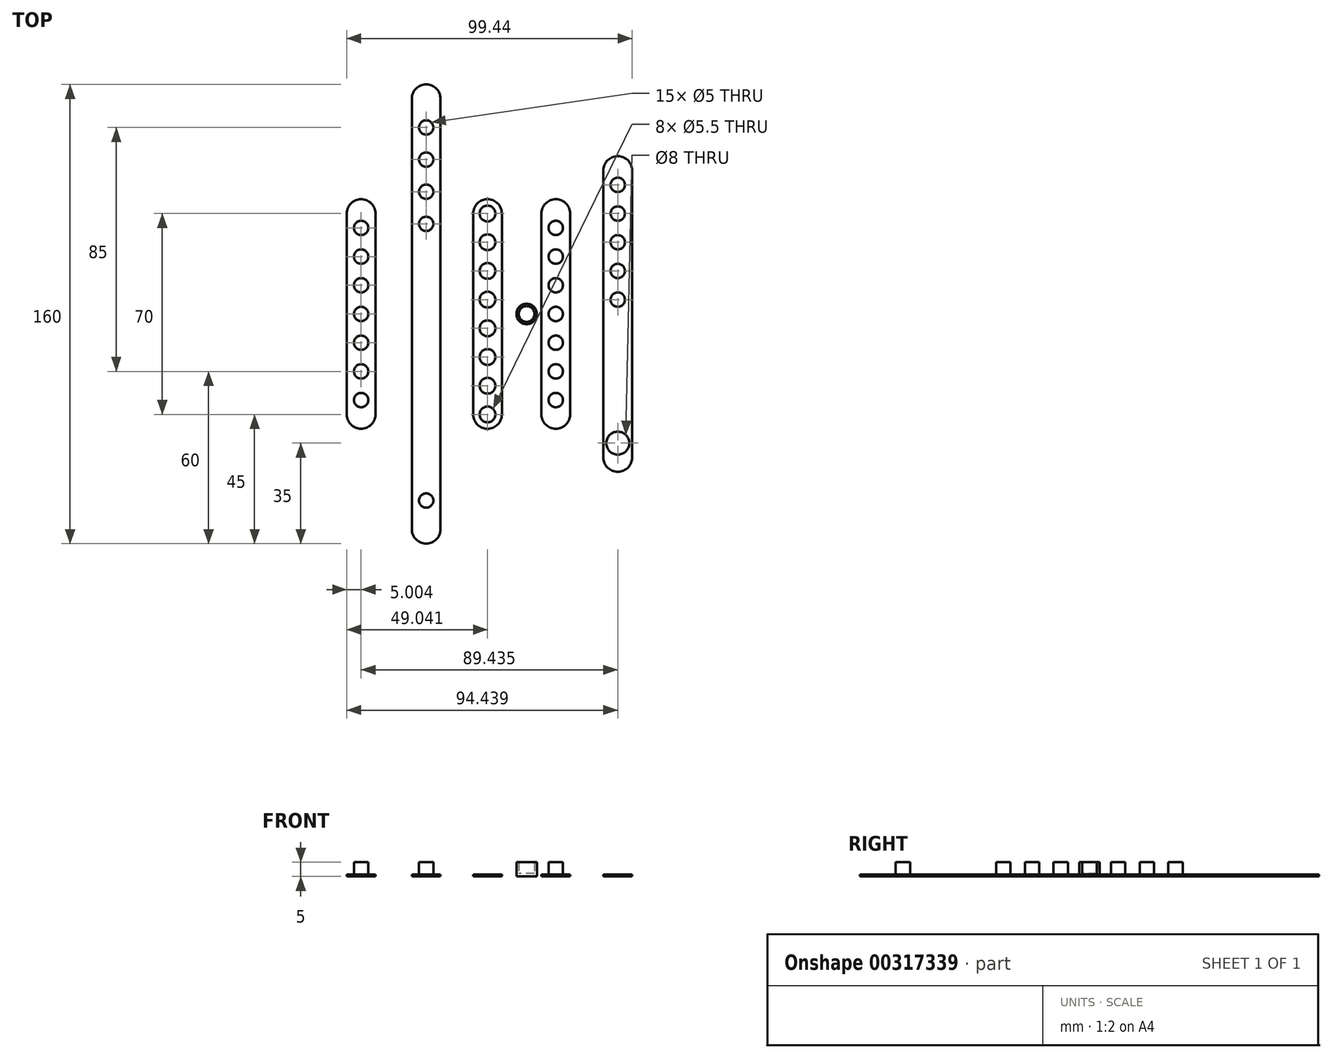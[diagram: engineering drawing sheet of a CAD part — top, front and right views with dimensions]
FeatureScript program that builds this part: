
annotation { "Feature Type Name" : "Feature", "Feature Type Description" : "" }
export const myFeature = defineFeature(function(context is Context, id is Id, definition is map)
    precondition{}
    {
        {
            var Q0;
            Q0=qCreatedBy(makeId("Top.planeOp"),FACE);
            var sketch = newSketch(context, id + "F0", { "sketchPlane" : qUnion([Q0])});
            skLineSegment(sketch, "E0", {"start": v(-40, 75) * mm, "end": v(-40, -75) * mm});
            skLineSegment(sketch, "E1", {"start": v(-40, -75) * mm, "end": v(-30, -75) * mm});
            skLineSegment(sketch, "E2", {"start": v(-30, -75) * mm, "end": v(-30, 75) * mm});
            skLineSegment(sketch, "E3", {"start": v(-30, 75) * mm, "end": v(-40, 75) * mm});
            skArc(sketch, "E4", {"start": v(-30, -75) * mm, "mid": v(-35, -80) * mm, "end": v(-40, -75) * mm});
            skArc(sketch, "E5", {"start": v(-30, 75) * mm, "mid": v(-35, 80) * mm, "end": v(-40, 75) * mm});
            skCircle(sketch, "E6", {"center": v(-35, -65) * mm, "radius": 2.5 * mm});
            skCircle(sketch, "E7", {"center": v(-35, 65) * mm, "radius": 2.5 * mm});
            skPoint(sketch, "E8", {"position": v(-30, 0) * mm});
            skLineSegment(sketch, "E9", {"start": v(-35, 75) * mm, "end": v(-35, 65) * mm, "construction": true});
            skLineSegment(sketch, "E10", {"start": v(-35, -65) * mm, "end": v(-35, -75) * mm, "construction": true});
            skCircle(sketch, "E11.0.1.0", {"center": v(-35, 53.8) * mm, "radius": 2.5 * mm});
            skLineSegment(sketch, "E11.0.1.1", {"start": v(-35, 63.8) * mm, "end": v(-35, 53.8) * mm, "construction": true});
            skCircle(sketch, "E11.0.2.0", {"center": v(-35, 42.6) * mm, "radius": 2.5 * mm});
            skLineSegment(sketch, "E11.0.2.1", {"start": v(-35, 52.6) * mm, "end": v(-35, 42.6) * mm, "construction": true});
            skCircle(sketch, "E11.0.3.0", {"center": v(-35, 31.4) * mm, "radius": 2.5 * mm});
            skLineSegment(sketch, "E11.0.3.1", {"start": v(-35, 41.4) * mm, "end": v(-35, 31.4) * mm, "construction": true});
            skLineSegment(sketch, "E11.direction1", {"start": v(-35, 65) * mm, "end": v(-10, 65) * mm, "construction": true});
            skLineSegment(sketch, "E11.direction2", {"start": v(-35, 65) * mm, "end": v(-35, 53.8) * mm, "construction": true});
            skLineSegment(sketch, "E12", {"start": v(-52.67, 35) * mm, "end": v(-52.67, -35) * mm});
            skLineSegment(sketch, "E13", {"start": v(-52.67, -35) * mm, "end": v(-62.67, -35) * mm});
            skLineSegment(sketch, "E14", {"start": v(-62.67, -35) * mm, "end": v(-62.67, 35) * mm});
            skLineSegment(sketch, "E15", {"start": v(-62.67, 35) * mm, "end": v(-52.67, 35) * mm});
            skArc(sketch, "E16", {"start": v(-52.67, 35) * mm, "mid": v(-57.67, 40) * mm, "end": v(-62.67, 35) * mm});
            skArc(sketch, "E17", {"start": v(-62.67, -35) * mm, "mid": v(-57.67, -40) * mm, "end": v(-52.67, -35) * mm});
            skCircle(sketch, "E18", {"center": v(-57.67, -30) * mm, "radius": 2.5 * mm});
            skCircle(sketch, "E19", {"center": v(-57.67, 30) * mm, "radius": 2.5 * mm});
            skLineSegment(sketch, "E20", {"start": v(-57.67, -35) * mm, "end": v(-57.67, -30) * mm, "construction": true});
            skLineSegment(sketch, "E21", {"start": v(-57.67, 30) * mm, "end": v(-57.67, 35) * mm, "construction": true});
            skCircle(sketch, "E22.0.1.0", {"center": v(-57.67, 20) * mm, "radius": 2.5 * mm});
            skCircle(sketch, "E22.0.2.0", {"center": v(-57.67, 10) * mm, "radius": 2.5 * mm});
            skCircle(sketch, "E22.0.3.0", {"center": v(-57.67, 0) * mm, "radius": 2.5 * mm});
            skCircle(sketch, "E22.0.4.0", {"center": v(-57.67, -10) * mm, "radius": 2.5 * mm});
            skLineSegment(sketch, "E22.direction1", {"start": v(-57.67, 30) * mm, "end": v(-32.67, 30) * mm, "construction": true});
            skLineSegment(sketch, "E22.direction2", {"start": v(-57.67, 30) * mm, "end": v(-57.67, 20) * mm, "construction": true});
            skPoint(sketch, "E23", {"position": v(-52.67, 0) * mm});
            skCircle(sketch, "E24.0.0.5", {"center": v(-57.67, -20) * mm, "radius": 2.5 * mm});
            skLineSegment(sketch, "E25", {"start": v(36.77, 50) * mm, "end": v(36.77, -50) * mm});
            skLineSegment(sketch, "E26", {"start": v(36.77, -50) * mm, "end": v(26.77, -50) * mm});
            skLineSegment(sketch, "E27", {"start": v(26.77, -50) * mm, "end": v(26.77, 50) * mm});
            skLineSegment(sketch, "E28", {"start": v(26.77, 50) * mm, "end": v(36.77, 50) * mm});
            skArc(sketch, "E29", {"start": v(36.77, 50) * mm, "mid": v(31.77, 55) * mm, "end": v(26.77, 50) * mm});
            skArc(sketch, "E30", {"start": v(26.77, -50) * mm, "mid": v(31.77, -55) * mm, "end": v(36.77, -50) * mm});
            skCircle(sketch, "E31", {"center": v(31.77, -45) * mm, "radius": 4 * mm});
            skCircle(sketch, "E32", {"center": v(31.77, 45) * mm, "radius": 2.5 * mm});
            skLineSegment(sketch, "E33", {"start": v(31.77, -50) * mm, "end": v(31.77, -45) * mm, "construction": true});
            skLineSegment(sketch, "E34", {"start": v(31.77, 45) * mm, "end": v(31.77, 50) * mm, "construction": true});
            skPoint(sketch, "E35", {"position": v(36.77, 0) * mm});
            skCircle(sketch, "E36.0.1.0", {"center": v(31.77, 35) * mm, "radius": 2.5 * mm});
            skCircle(sketch, "E36.0.2.0", {"center": v(31.77, 25) * mm, "radius": 2.5 * mm});
            skCircle(sketch, "E36.0.3.0", {"center": v(31.77, 15) * mm, "radius": 2.5 * mm});
            skCircle(sketch, "E36.0.4.0", {"center": v(31.77, 5) * mm, "radius": 2.5 * mm});
            skLineSegment(sketch, "E36.direction1", {"start": v(31.77, 45) * mm, "end": v(56.77, 45) * mm, "construction": true});
            skLineSegment(sketch, "E36.direction2", {"start": v(31.77, 45) * mm, "end": v(31.77, 35) * mm, "construction": true});
            skLineSegment(sketch, "E37", {"start": v(-8.63, 35) * mm, "end": v(-8.63, -35) * mm});
            skLineSegment(sketch, "E38", {"start": v(-8.63, -35) * mm, "end": v(-18.63, -35) * mm});
            skLineSegment(sketch, "E39", {"start": v(-18.63, -35) * mm, "end": v(-18.63, 35) * mm});
            skLineSegment(sketch, "E40", {"start": v(-18.63, 35) * mm, "end": v(-8.63, 35) * mm});
            skArc(sketch, "E41", {"start": v(-8.63, 35) * mm, "mid": v(-13.63, 40) * mm, "end": v(-18.63, 35) * mm});
            skArc(sketch, "E42", {"start": v(-18.63, -35) * mm, "mid": v(-13.63, -40) * mm, "end": v(-8.63, -35) * mm});
            skCircle(sketch, "E43", {"center": v(-13.63, -35) * mm, "radius": 2.75 * mm});
            skCircle(sketch, "E44", {"center": v(-13.63, 35) * mm, "radius": 2.75 * mm});
            skLineSegment(sketch, "E45", {"start": v(-13.63, -35) * mm, "end": v(-13.63, -35) * mm});
            skLineSegment(sketch, "E46", {"start": v(-13.63, 35) * mm, "end": v(-13.63, 35) * mm});
            skPoint(sketch, "E47", {"position": v(-8.63, 0) * mm});
            skLineSegment(sketch, "E48", {"start": v(15.17, 35) * mm, "end": v(15.17, -35) * mm});
            skLineSegment(sketch, "E49", {"start": v(15.17, -35) * mm, "end": v(5.17, -35) * mm});
            skLineSegment(sketch, "E50", {"start": v(5.17, -35) * mm, "end": v(5.17, 35) * mm});
            skLineSegment(sketch, "E51", {"start": v(5.17, 35) * mm, "end": v(15.17, 35) * mm});
            skArc(sketch, "E52", {"start": v(15.17, 35) * mm, "mid": v(10.17, 40) * mm, "end": v(5.17, 35) * mm});
            skArc(sketch, "E53", {"start": v(5.17, -35) * mm, "mid": v(10.17, -40) * mm, "end": v(15.17, -35) * mm});
            skCircle(sketch, "E54", {"center": v(10.17, -30) * mm, "radius": 2.5 * mm});
            skCircle(sketch, "E55", {"center": v(10.17, 30) * mm, "radius": 2.5 * mm});
            skLineSegment(sketch, "E56", {"start": v(10.17, -35) * mm, "end": v(10.17, -30) * mm, "construction": true});
            skLineSegment(sketch, "E57", {"start": v(10.17, 30) * mm, "end": v(10.17, 35) * mm, "construction": true});
            skCircle(sketch, "E58.0.1.0", {"center": v(10.17, 20) * mm, "radius": 2.5 * mm});
            skCircle(sketch, "E58.0.2.0", {"center": v(10.17, 10) * mm, "radius": 2.5 * mm});
            skCircle(sketch, "E58.0.3.0", {"center": v(10.17, 0) * mm, "radius": 2.5 * mm});
            skCircle(sketch, "E58.0.4.0", {"center": v(10.17, -10) * mm, "radius": 2.5 * mm});
            skLineSegment(sketch, "E58.direction2", {"start": v(10.17, 30) * mm, "end": v(10.17, 20) * mm, "construction": true});
            skPoint(sketch, "E59", {"position": v(15.17, 0) * mm});
            skCircle(sketch, "E60.0.0.5", {"center": v(10.17, -20) * mm, "radius": 2.5 * mm});
            skCircle(sketch, "E61", {"center": v(0, 0) * mm, "radius": 2.75 * mm});
            skCircle(sketch, "E62", {"center": v(0, 0) * mm, "radius": 3.55 * mm});
            skCircle(sketch, "E63.0.1.0", {"center": v(-13.63, 25) * mm, "radius": 2.75 * mm});
            skCircle(sketch, "E63.0.2.0", {"center": v(-13.63, 15) * mm, "radius": 2.75 * mm});
            skCircle(sketch, "E63.0.3.0", {"center": v(-13.63, 5) * mm, "radius": 2.75 * mm});
            skCircle(sketch, "E63.0.4.0", {"center": v(-13.63, -5) * mm, "radius": 2.75 * mm});
            skCircle(sketch, "E63.0.5.0", {"center": v(-13.63, -15) * mm, "radius": 2.75 * mm});
            skCircle(sketch, "E63.0.6.0", {"center": v(-13.63, -25) * mm, "radius": 2.75 * mm});
            skLineSegment(sketch, "E63.direction1", {"start": v(-13.63, 35) * mm, "end": v(-3.63, 35) * mm, "construction": true});
            skLineSegment(sketch, "E63.direction2", {"start": v(-13.63, 35) * mm, "end": v(-13.63, 25) * mm, "construction": true});
            skSolve(sketch);
        }
        {
            var Q0;
            Q0=makeQuery(id+"F0.imprint","IMPRINT",FACE,{"disambiguationData":[TD([[makeQuery(id+"F0.imprint","IMPRINT",EDGE,{"derivedFrom":sQuery(id+"F0.wireOp",EDGE,"E0")}),1.0]])]});
            var Q1;
            Q1=makeQuery(id+"F0.imprint","IMPRINT",FACE,{"disambiguationData":[TD([[makeQuery(id+"F0.imprint","IMPRINT",EDGE,{"derivedFrom":sQuery(id+"F0.wireOp",EDGE,"E1")}),-1.0]])]});
            var Q2;
            Q2=makeQuery(id+"F0.imprint","IMPRINT",FACE,{"disambiguationData":[TD([[makeQuery(id+"F0.imprint","IMPRINT",EDGE,{"derivedFrom":sQuery(id+"F0.wireOp",EDGE,"E3")}),-1.0]])]});
            extrude(context, id + "F1", {"entities" : qUnion([Q0, Q1, Q2]), "depth" : .7 * mm});
        }
        {
            var Q0;
            Q0=makeQuery(id+"F0.imprint","IMPRINT",FACE,{"disambiguationData":[TD([[makeQuery(id+"F0.imprint","IMPRINT",EDGE,{"derivedFrom":sQuery(id+"F0.wireOp",EDGE,"E6")}),1.0]])]});
            extrude(context, id + "F2", {"entities" : qUnion([Q0]), "operationType" : NewBodyOperationType.ADD, "depth" : 5 * mm});
        }
        {
            var Q0;
            Q0=makeQuery(id+"F0.imprint","IMPRINT",FACE,{"disambiguationData":[TD([[makeQuery(id+"F0.imprint","IMPRINT",EDGE,{"derivedFrom":sQuery(id+"F0.wireOp",EDGE,"E15")}),1.0]])]});
            var Q1;
            Q1=makeQuery(id+"F0.imprint","IMPRINT",FACE,{"disambiguationData":[TD([[makeQuery(id+"F0.imprint","IMPRINT",EDGE,{"derivedFrom":sQuery(id+"F0.wireOp",EDGE,"E12")}),-1.0]])]});
            var Q2;
            Q2=makeQuery(id+"F0.imprint","IMPRINT",FACE,{"disambiguationData":[TD([[makeQuery(id+"F0.imprint","IMPRINT",EDGE,{"derivedFrom":sQuery(id+"F0.wireOp",EDGE,"E13")}),1.0]])]});
            extrude(context, id + "F3", {"entities" : qUnion([Q0, Q1, Q2]), "depth" : .7 * mm});
        }
        {
            var Q0;
            Q0=makeQuery(id+"F0.imprint","IMPRINT",FACE,{"disambiguationData":[TD([[makeQuery(id+"F0.imprint","IMPRINT",EDGE,{"derivedFrom":sQuery(id+"F0.wireOp",EDGE,"E18")}),1.0]])]});
            extrude(context, id + "F4", {"entities" : qUnion([Q0]), "operationType" : NewBodyOperationType.ADD, "depth" : 5 * mm});
        }
        {
            var Q0;
            Q0=makeQuery(id+"F0.imprint","IMPRINT",FACE,{"disambiguationData":[TD([[makeQuery(id+"F0.imprint","IMPRINT",EDGE,{"derivedFrom":sQuery(id+"F0.wireOp",EDGE,"E25")}),-1.0]])]});
            var Q1;
            Q1=makeQuery(id+"F0.imprint","IMPRINT",FACE,{"disambiguationData":[TD([[makeQuery(id+"F0.imprint","IMPRINT",EDGE,{"derivedFrom":sQuery(id+"F0.wireOp",EDGE,"E26")}),1.0]])]});
            var Q2;
            Q2=makeQuery(id+"F0.imprint","IMPRINT",FACE,{"disambiguationData":[TD([[makeQuery(id+"F0.imprint","IMPRINT",EDGE,{"derivedFrom":sQuery(id+"F0.wireOp",EDGE,"E28")}),1.0]])]});
            extrude(context, id + "F5", {"entities" : qUnion([Q0, Q1, Q2]), "depth" : .7 * mm});
        }
        {
            var Q0;
            Q0=makeQuery(id+"F0.imprint","IMPRINT",FACE,{"disambiguationData":[TD([[makeQuery(id+"F0.imprint","IMPRINT",EDGE,{"derivedFrom":sQuery(id+"F0.wireOp",EDGE,"E40")}),1.0]])]});
            var Q1;
            Q1=makeQuery(id+"F0.imprint","IMPRINT",FACE,{"disambiguationData":[TD([[makeQuery(id+"F0.imprint","IMPRINT",EDGE,{"derivedFrom":sQuery(id+"F0.wireOp",EDGE,"E37")}),-1.0]])]});
            var Q2;
            Q2=makeQuery(id+"F0.imprint","IMPRINT",FACE,{"disambiguationData":[TD([[makeQuery(id+"F0.imprint","IMPRINT",EDGE,{"derivedFrom":sQuery(id+"F0.wireOp",EDGE,"E38")}),1.0]])]});
            extrude(context, id + "F6", {"entities" : qUnion([Q0, Q1, Q2]), "depth" : .7 * mm});
        }
        {
            var Q0;
            Q0=makeQuery(id+"F0.imprint","IMPRINT",FACE,{"disambiguationData":[TD([[makeQuery(id+"F0.imprint","IMPRINT",EDGE,{"derivedFrom":sQuery(id+"F0.wireOp",EDGE,"E51")}),1.0]])]});
            var Q1;
            Q1=makeQuery(id+"F0.imprint","IMPRINT",FACE,{"disambiguationData":[TD([[makeQuery(id+"F0.imprint","IMPRINT",EDGE,{"derivedFrom":sQuery(id+"F0.wireOp",EDGE,"E48")}),-1.0]])]});
            var Q2;
            Q2=makeQuery(id+"F0.imprint","IMPRINT",FACE,{"disambiguationData":[TD([[makeQuery(id+"F0.imprint","IMPRINT",EDGE,{"derivedFrom":sQuery(id+"F0.wireOp",EDGE,"E49")}),1.0]])]});
            extrude(context, id + "F7", {"entities" : qUnion([Q0, Q1, Q2]), "depth" : .7 * mm});
        }
        {
            var Q0;
            Q0=makeQuery(id+"F0.imprint","IMPRINT",FACE,{"disambiguationData":[TD([[makeQuery(id+"F0.imprint","IMPRINT",EDGE,{"derivedFrom":sQuery(id+"F0.wireOp",EDGE,"E55")}),1.0]])]});
            var Q1;
            Q1=makeQuery(id+"F0.imprint","IMPRINT",FACE,{"disambiguationData":[TD([[makeQuery(id+"F0.imprint","IMPRINT",EDGE,{"derivedFrom":sQuery(id+"F0.wireOp",EDGE,"E58.0.1.0")}),1.0]])]});
            var Q2;
            Q2=makeQuery(id+"F0.imprint","IMPRINT",FACE,{"disambiguationData":[TD([[makeQuery(id+"F0.imprint","IMPRINT",EDGE,{"derivedFrom":sQuery(id+"F0.wireOp",EDGE,"E58.0.2.0")}),1.0]])]});
            var Q3;
            Q3=makeQuery(id+"F0.imprint","IMPRINT",FACE,{"disambiguationData":[TD([[makeQuery(id+"F0.imprint","IMPRINT",EDGE,{"derivedFrom":sQuery(id+"F0.wireOp",EDGE,"E58.0.3.0")}),1.0]])]});
            var Q4;
            Q4=makeQuery(id+"F0.imprint","IMPRINT",FACE,{"disambiguationData":[TD([[makeQuery(id+"F0.imprint","IMPRINT",EDGE,{"derivedFrom":sQuery(id+"F0.wireOp",EDGE,"E58.0.4.0")}),1.0]])]});
            var Q5;
            Q5=makeQuery(id+"F0.imprint","IMPRINT",FACE,{"disambiguationData":[TD([[makeQuery(id+"F0.imprint","IMPRINT",EDGE,{"derivedFrom":sQuery(id+"F0.wireOp",EDGE,"E60.0.0.5")}),1.0]])]});
            var Q6;
            Q6=makeQuery(id+"F0.imprint","IMPRINT",FACE,{"disambiguationData":[TD([[makeQuery(id+"F0.imprint","IMPRINT",EDGE,{"derivedFrom":sQuery(id+"F0.wireOp",EDGE,"E54")}),1.0]])]});
            extrude(context, id + "F8", {"entities" : qUnion([Q0, Q1, Q2, Q3, Q4, Q5, Q6]), "operationType" : NewBodyOperationType.ADD, "depth" : 5 * mm});
        }
        {
            var Q0;
            Q0=makeQuery(id+"F0.imprint","IMPRINT",FACE,{"disambiguationData":[TD([[makeQuery(id+"F0.imprint","IMPRINT",EDGE,{"derivedFrom":sQuery(id+"F0.wireOp",EDGE,"E61")}),-1.0]])]});
            extrude(context, id + "F9", {"entities" : qUnion([Q0]), "depth" : 5 * mm});
        }
        {
            var Q0;
            Q0=makeQuery(id+"F0.imprint","IMPRINT",FACE,{"disambiguationData":[TD([[makeQuery(id+"F0.imprint","IMPRINT",EDGE,{"derivedFrom":sQuery(id+"F0.wireOp",EDGE,"E61")}),1.0]])]});
            extrude(context, id + "F10", {"entities" : qUnion([Q0]), "operationType" : NewBodyOperationType.ADD, "depth" : 1 * mm});
        }
    });
